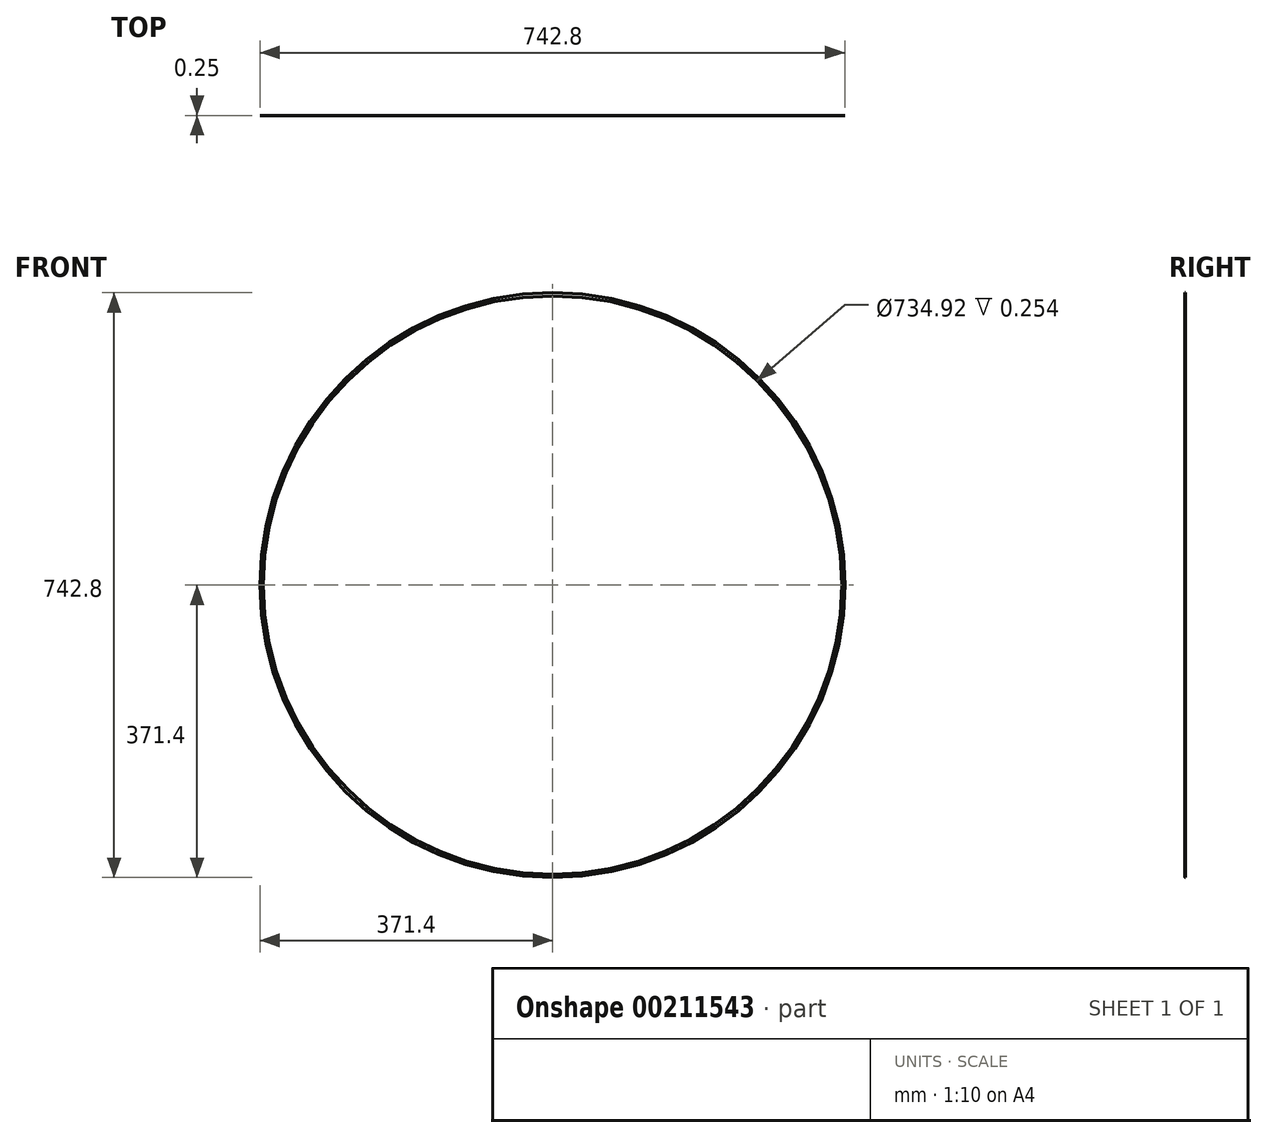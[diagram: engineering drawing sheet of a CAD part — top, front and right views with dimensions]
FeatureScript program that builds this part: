
annotation { "Feature Type Name" : "Feature", "Feature Type Description" : "" }
export const myFeature = defineFeature(function(context is Context, id is Id, definition is map)
    precondition{}
    {
        {
            var Q0;
            Q0=qCreatedBy(makeId("Front.planeOp"),FACE);
            var sketch = newSketch(context, id + "F0", { "sketchPlane" : qUnion([Q0])});
            skCircle(sketch, "E0", {"center": v(0, 0) * mm, "radius": 371.4 * mm});
            skSolve(sketch);
        }
        {
            var Q0;
            Q0 = qSketchRegion(id + "F0", true);
            extrude(context, id + "F1", {"entities" : qUnion([Q0]), "oppositeDirection" : true, "depth" : 0.25 * mm});
        }
        {
            var Q0;
            Q0=makeQuery(id+"F1.opExtrude","CAP_FACE",FACE,{"disambiguationData":[OSD([sQuery(id+"F0.wireOp",EDGE,"E0")])],"isStart":true});
            var sketch = newSketch(context, id + "F2", { "sketchPlane" : qUnion([Q0])});
            skCircle(sketch, "E1", {"center": v(0, 0) * mm, "radius": 367.46 * mm});
            skSolve(sketch);
        }
        {
            var Q0;
            Q0 = qSketchRegion(id + "F2", true);
            extrude(context, id + "F3", {"entities" : qUnion([Q0]), "operationType" : NewBodyOperationType.REMOVE, "oppositeDirection" : true, "depth" : 152.4 * mm});
        }
    });
